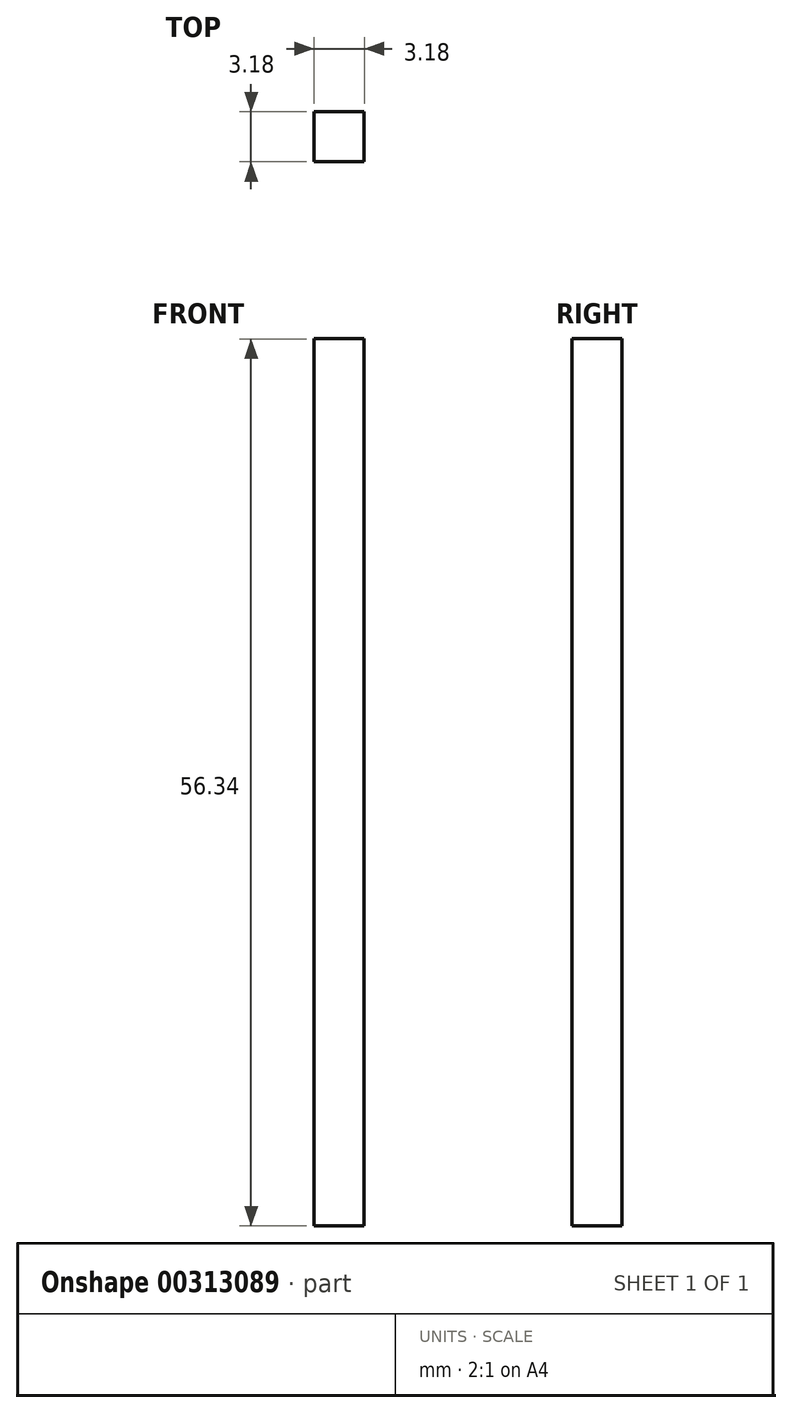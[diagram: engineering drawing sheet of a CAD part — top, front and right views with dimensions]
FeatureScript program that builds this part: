
annotation { "Feature Type Name" : "Feature", "Feature Type Description" : "" }
export const myFeature = defineFeature(function(context is Context, id is Id, definition is map)
    precondition{}
    {
        {
            var Q0;
            Q0=qCreatedBy(makeId("Top.planeOp"),FACE);
            var sketch = newSketch(context, id + "F0", { "sketchPlane" : qUnion([Q0])});
            skLineSegment(sketch, "E0.bottom", {"start": v(1.59, 1.59) * mm, "end": v(-1.59, 1.59) * mm});
            skLineSegment(sketch, "E0.top", {"start": v(1.59, -1.59) * mm, "end": v(-1.59, -1.59) * mm});
            skLineSegment(sketch, "E0.left", {"start": v(1.59, 1.59) * mm, "end": v(1.59, -1.59) * mm});
            skLineSegment(sketch, "E0.right", {"start": v(-1.59, 1.59) * mm, "end": v(-1.59, -1.59) * mm});
            skPoint(sketch, "E0.middle", {"position": v(0, 0) * mm});
            skSolve(sketch);
        }
        {
            var Q0;
            Q0=qSketchRegion(id+"F0",true);
            extrude(context, id + "F1", {"entities" : qUnion([Q0]), "endBound" : BoundingType.SYMMETRIC, "depth" : 56.35 * mm});
        }
    });
